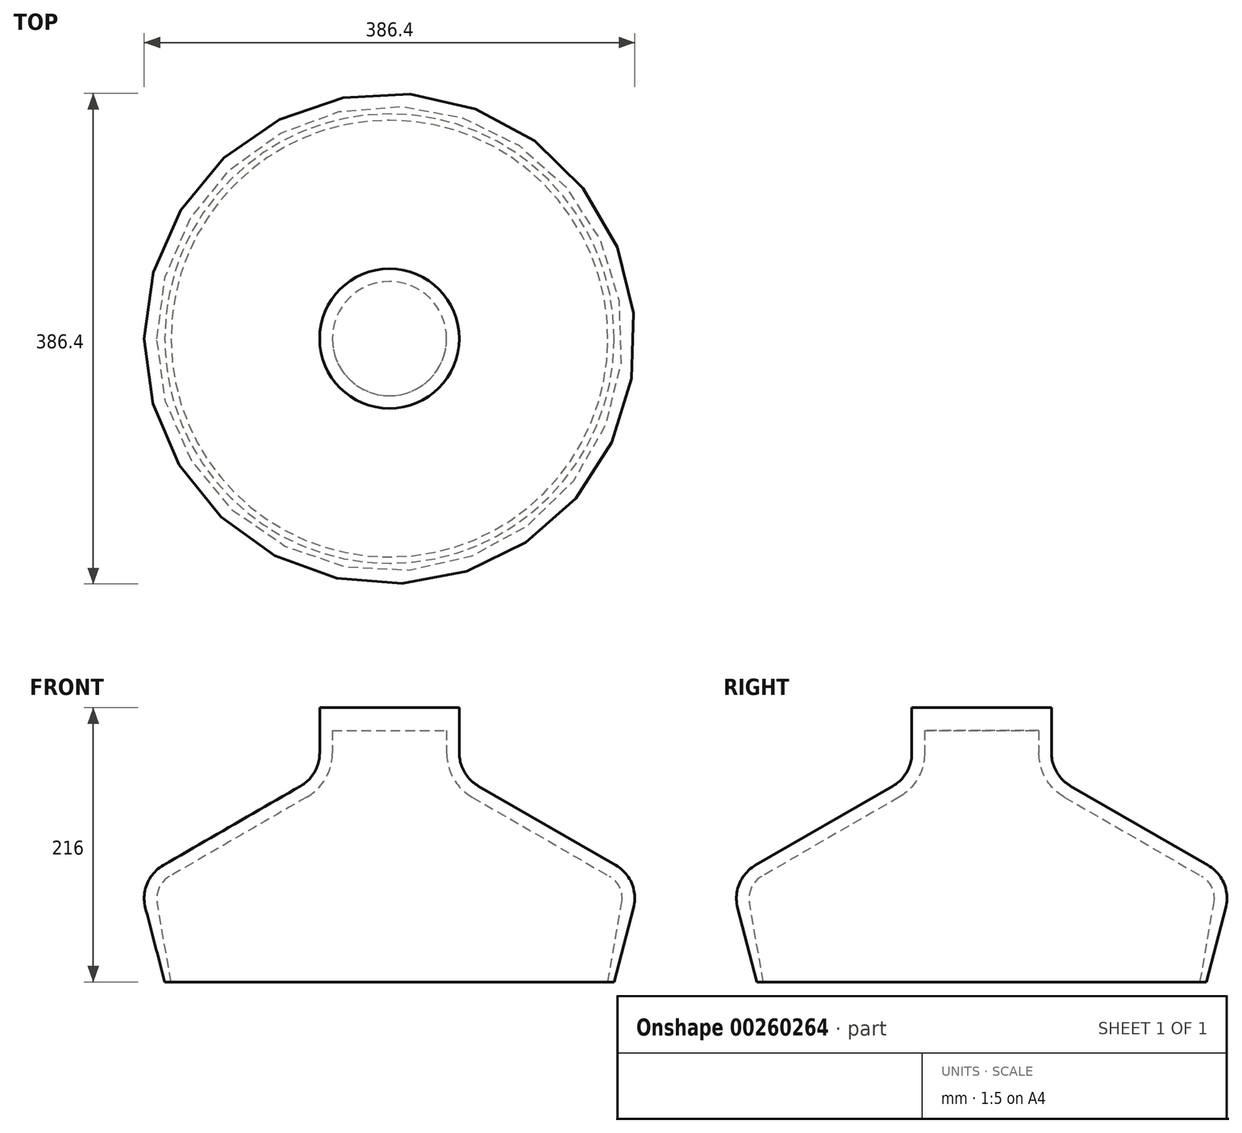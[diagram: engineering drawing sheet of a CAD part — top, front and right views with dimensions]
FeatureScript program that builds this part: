
annotation { "Feature Type Name" : "Feature", "Feature Type Description" : "" }
export const myFeature = defineFeature(function(context is Context, id is Id, definition is map)
    precondition{}
    {
        {
            var Q0;
            Q0=qCreatedBy(makeId("Front.planeOp"),FACE);
            var sketch = newSketch(context, id + "F0", { "sketchPlane" : qUnion([Q0])});
            skLineSegment(sketch, "E0", {"start": v(0, 0) * mm, "end": v(0, 198) * mm, "construction": true});
            skLineSegment(sketch, "E1", {"start": v(0, 198) * mm, "end": v(0, 216) * mm});
            skPoint(sketch, "E1.endSnap0", {"position": v(0, 99) * mm});
            skLineSegment(sketch, "E2", {"start": v(0, 216) * mm, "end": v(55, 216) * mm});
            skLineSegment(sketch, "E3", {"start": v(55, 216) * mm, "end": v(55, 163) * mm});
            skLineSegment(sketch, "E4", {"start": v(55, 163) * mm, "end": v(198, 80.44) * mm});
            skLineSegment(sketch, "E5", {"start": v(198, 80.44) * mm, "end": v(177, 0) * mm});
            skLineSegment(sketch, "E6", {"start": v(177, 0) * mm, "end": v(172, 0) * mm});
            skLineSegment(sketch, "E7", {"start": v(172, 0) * mm, "end": v(185.3, 76.22) * mm});
            skLineSegment(sketch, "E8", {"start": v(185.3, 76.22) * mm, "end": v(45, 157.23) * mm});
            skLineSegment(sketch, "E9", {"start": v(45, 157.23) * mm, "end": v(45, 198) * mm});
            skLineSegment(sketch, "E10", {"start": v(45, 198) * mm, "end": v(0, 198) * mm});
            skCircle(sketch, "E11", {"center": v(163.2, 65.9) * mm, "radius": 20 * mm, "construction": true});
            skCircle(sketch, "E12", {"center": v(163.2, 65.9) * mm, "radius": 30 * mm, "construction": true});
            skSolve(sketch);
        }
        {
            var Q0;
            Q0=makeQuery(id+"F0.imprint","IMPRINT",FACE,{"disambiguationData":[TD([[makeQuery(id+"F0.imprint","IMPRINT",EDGE,{"derivedFrom":sQuery(id+"F0.wireOp",EDGE,"E1")}),-1.0]])]});
            var Q1;
            Q1=sQuery(id+"F0.wireOp",EDGE,"E0");
            revolve(context, id + "F1", {"entities" : qUnion([Q0]), "axis" : qUnion([Q1]), "revolveType" : RevolveType.FULL});
        }
        {
            var Q0;
            Q0=makeQuery(id+"F1.opRevolve","SWEPT_EDGE",EDGE,{"disambiguationData":[OSD([sQuery(id+"F0.wireOp",EDGE,"E7"),sQuery(id+"F0.wireOp",EDGE,"E8")])]});
            fillet(context, id + "F2", {"entities" : qUnion([Q0]), "radius" : 20 * mm, "tangentPropagation" : true, "allowEdgeOverflow" : false});
        }
        {
            var Q0;
            Q0=makeQuery(id+"F1.opRevolve","SWEPT_EDGE",EDGE,{"disambiguationData":[OSD([sQuery(id+"F0.wireOp",EDGE,"E4"),sQuery(id+"F0.wireOp",EDGE,"E5")])]});
            var Q1;
            Q1=makeQuery(id+"F1.opRevolve","SWEPT_EDGE",EDGE,{"disambiguationData":[OSD([sQuery(id+"F0.wireOp",EDGE,"E3"),sQuery(id+"F0.wireOp",EDGE,"E4")])]});
            fillet(context, id + "F3", {"entities" : qUnion([Q0, Q1]), "radius" : 30 * mm, "tangentPropagation" : true, "allowEdgeOverflow" : false});
        }
        {
            var Q0;
            Q0=makeQuery(id+"F1.opRevolve","SWEPT_EDGE",EDGE,{"disambiguationData":[OSD([sQuery(id+"F0.wireOp",EDGE,"E8"),sQuery(id+"F0.wireOp",EDGE,"E9")])]});
            fillet(context, id + "F4", {"entities" : qUnion([Q0]), "radius" : 40 * mm, "tangentPropagation" : true, "allowEdgeOverflow" : false});
        }
    });
